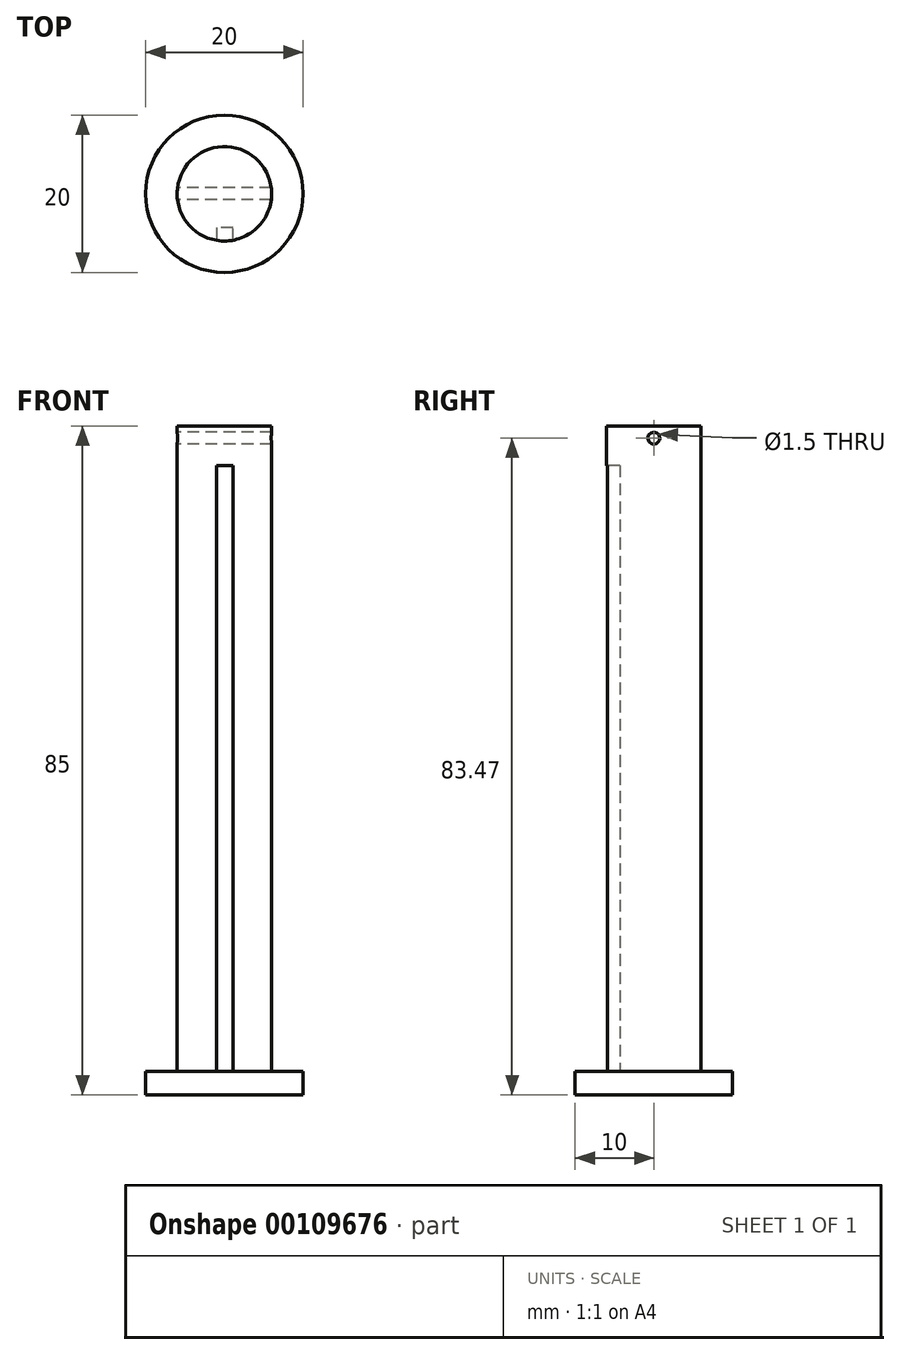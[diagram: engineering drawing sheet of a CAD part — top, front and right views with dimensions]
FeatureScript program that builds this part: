
annotation { "Feature Type Name" : "Feature", "Feature Type Description" : "" }
export const myFeature = defineFeature(function(context is Context, id is Id, definition is map)
    precondition{}
    {
        {
            var Q0;
            Q0=qCreatedBy(makeId("Top.planeOp"),FACE);
            var sketch = newSketch(context, id + "F0", { "sketchPlane" : qUnion([Q0])});
            skCircle(sketch, "E0", {"center": v(0, 0) * mm, "radius": 6 * mm});
            skLineSegment(sketch, "E1", {"start": v(1.1, -5.9) * mm, "end": v(1.1, -4.32) * mm});
            skLineSegment(sketch, "E2", {"start": v(1.1, -4.32) * mm, "end": v(-1, -4.32) * mm});
            skLineSegment(sketch, "E3", {"start": v(-1, -4.32) * mm, "end": v(-1, -5.91) * mm});
            skLineSegment(sketch, "E4", {"start": v(0, -4.32) * mm, "end": v(0, -6) * mm});
            skCircle(sketch, "E5", {"center": v(0, 0) * mm, "radius": 10 * mm});
            skSolve(sketch);
        }
        {
            var Q0;
            Q0=makeQuery(id+"F0.imprint","IMPRINT",FACE,{"disambiguationData":[TD([[makeQuery(id+"F0.imprint","IMPRINT",EDGE,{"derivedFrom":sQuery(id+"F0.wireOp",EDGE,"E0")}),1.0]])]});
            var Q1;
            {var subQ3=sQuery(id+"F0.wireOp",EDGE,"E1");Q1=makeQuery(id+"F0.imprint","IMPRINT",FACE,{"disambiguationData":[TD([[makeQuery(id+"F0.imprint","IMPRINT",EDGE,{"derivedFrom":subQ3}),-1.0]])]});}
            extrude(context, id + "F1", {"entities" : qUnion([Q0, Q1]), "depth" : 85 * mm});
        }
        {
            var Q0;
            Q0=makeQuery(id+"F0.imprint","IMPRINT",FACE,{"disambiguationData":[TD([[makeQuery(id+"F0.imprint","IMPRINT",EDGE,{"derivedFrom":sQuery(id+"F0.wireOp",EDGE,"E5")}),1.0]])]});
            extrude(context, id + "F2", {"entities" : qUnion([Q0]), "operationType" : NewBodyOperationType.ADD, "depth" : 3 * mm});
        }
        {
            var Q0;
            Q0=qCreatedBy(makeId("Right.planeOp"),FACE);
            var sketch = newSketch(context, id + "F3", { "sketchPlane" : qUnion([Q0])});
            skLineSegment(sketch, "E6", {"start": v(-6, 78) * mm, "end": v(-6, 80.2) * mm});
            skLineSegment(sketch, "E7", {"start": v(6, 82.37) * mm, "end": v(6, 3) * mm});
            skLineSegment(sketch, "E8", {"start": v(6, 84.57) * mm, "end": v(6, 82.37) * mm});
            skLineSegment(sketch, "E9", {"start": v(6, 83.47) * mm, "end": v(-6, 83.47) * mm, "construction": true});
            skCircle(sketch, "E10", {"center": v(0, 83.47) * mm, "radius": 0.75 * mm});
            skLineSegment(sketch, "E11", {"start": v(6, 80) * mm, "end": v(6, 3) * mm});
            skLineSegment(sketch, "E12", {"start": v(-6, 3) * mm, "end": v(-6, 83) * mm});
            skLineSegment(sketch, "E13", {"start": v(6, 83) * mm, "end": v(6, 3) * mm});
            skLineSegment(sketch, "E14", {"start": v(-6, 80.2) * mm, "end": v(-6, 83) * mm});
            skSolve(sketch);
        }
        {
            var Q0;
            Q0 = qSketchRegion(id + "F3", true);
            extrude(context, id + "F4", {"entities" : qUnion([Q0]), "operationType" : NewBodyOperationType.REMOVE, "endBound" : BoundingType.SYMMETRIC, "depth" : 30 * mm});
        }
        {
            var Q0;
            {var subQ0=sQuery(id+"F0.wireOp",EDGE,"E3");Q0=makeQuery(id+"F0.imprint","IMPRINT",FACE,{"disambiguationData":[TD([[makeQuery(id+"F0.imprint","IMPRINT",EDGE,{"derivedFrom":subQ0}),1.0]])]});}
            var Q1;
            {var subQ0=sQuery(id+"F0.wireOp",EDGE,"E1");Q1=makeQuery(id+"F0.imprint","IMPRINT",FACE,{"disambiguationData":[TD([[makeQuery(id+"F0.imprint","IMPRINT",EDGE,{"derivedFrom":subQ0}),1.0]])]});}
            var Q2;
            Q2=makeQuery(id+"F2.opExtrude","CAP_FACE",FACE,{"disambiguationData":[OSD([sQuery(id+"F0.wireOp",EDGE,"E0"),sQuery(id+"F0.wireOp",EDGE,"E5")])],"isStart":false});
            extrude(context, id + "F5", {"entities" : qUnion([Q0, Q1]), "operationType" : NewBodyOperationType.REMOVE, "depth" : 80 * mm, "hasSecondDirection" : true, "secondDirectionBound" : SecondDirectionBoundingType.UP_TO_SURFACE, "secondDirectionOppositeDirection" : false, "secondDirectionBoundEntityFace" : qUnion([Q2]), "secondDirectionDepth" : 25 * mm});
        }
    });
